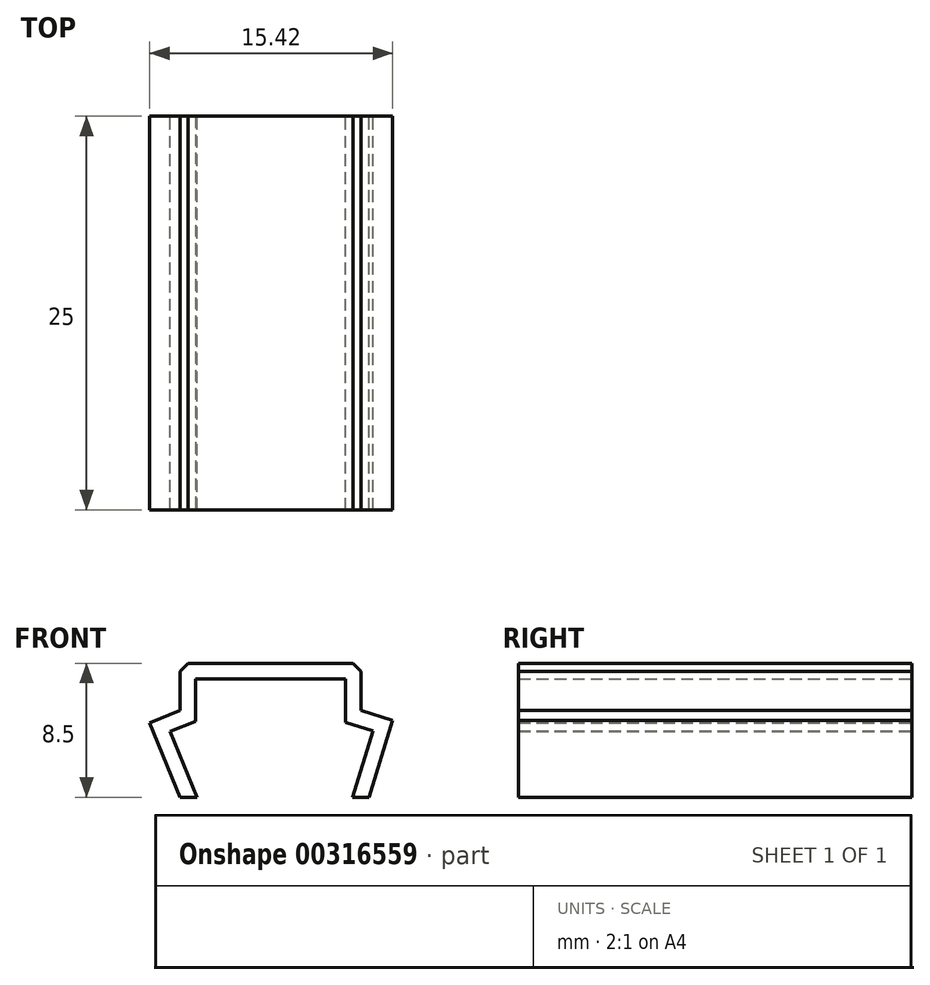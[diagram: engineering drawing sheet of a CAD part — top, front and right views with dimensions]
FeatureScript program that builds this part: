
annotation { "Feature Type Name" : "Feature", "Feature Type Description" : "" }
export const myFeature = defineFeature(function(context is Context, id is Id, definition is map)
    precondition{}
    {
        {
            var Q0;
            Q0=qCreatedBy(makeId("Front.planeOp"),FACE);
            var sketch = newSketch(context, id + "F0", { "sketchPlane" : qUnion([Q0])});
            skLineSegment(sketch, "E0.bottom", {"start": v(-0.8, 8.5) * mm, "end": v(9.7, 8.5) * mm});
            skLineSegment(sketch, "E0.left", {"start": v(-1.3, 8) * mm, "end": v(-1.3, 5.5) * mm});
            skLineSegment(sketch, "E0.right", {"start": v(10.2, 8) * mm, "end": v(10.2, 5.5) * mm});
            skLineSegment(sketch, "E1.top", {"start": v(-1.3, 0) * mm, "end": v(10.7, 0) * mm});
            skLineSegment(sketch, "E2", {"start": v(-3.23, 4.72) * mm, "end": v(-1.3, 0) * mm});
            skLineSegment(sketch, "E3", {"start": v(-1.3, 5.5) * mm, "end": v(-3.23, 4.72) * mm});
            skLineSegment(sketch, "E4", {"start": v(10.2, 5.5) * mm, "end": v(12.2, 4.89) * mm});
            skLineSegment(sketch, "E5", {"start": v(12.2, 4.89) * mm, "end": v(10.7, 0) * mm});
            skLineSegment(sketch, "E6", {"start": v(-1.3, 8) * mm, "end": v(-0.8, 8.5) * mm});
            skLineSegment(sketch, "E7", {"start": v(9.7, 8.5) * mm, "end": v(10.2, 8) * mm});
            skSolve(sketch);
        }
        {
            var Q0;
            Q0=makeQuery(id+"F0.imprint","IMPRINT",FACE,{"disambiguationData":[TD([[makeQuery(id+"F0.imprint","IMPRINT",EDGE,{"derivedFrom":sQuery(id+"F0.wireOp",EDGE,"E0.bottom")}),-1.0]])]});
            extrude(context, id + "F1", {"entities" : qUnion([Q0]), "depth" : 25 * mm});
        }
        {
            var Q0;
            Q0=makeQuery(id+"F1.opExtrude","CAP_FACE",FACE,{"disambiguationData":[OSD([sQuery(id+"F0.wireOp",EDGE,"E0.bottom"),sQuery(id+"F0.wireOp",EDGE,"E0.left"),sQuery(id+"F0.wireOp",EDGE,"E0.right"),sQuery(id+"F0.wireOp",EDGE,"E1.bottom"),sQuery(id+"F0.wireOp",EDGE,"E1.top"),sQuery(id+"F0.wireOp",EDGE,"0d6bb723-9a7b-4d77-b57e-2279504a17e3.trimOffspring"),sQuery(id+"F0.wireOp",EDGE,"19e43eaa-ee09-435e-811b-5a9f896a7d2e.filletArc"),sQuery(id+"F0.wireOp",EDGE,"6ffb7b8e-48f9-446f-8dbe-ae3deb286622.filletArc"),sQuery(id+"F0.wireOp",EDGE,"E2"),sQuery(id+"F0.wireOp",EDGE,"KxVvcCu0-cP9C-hDc2-rJ1g-qD9v42R25ilj")])],"isStart":false});
            var Q1;
            Q1=makeQuery(id+"F1.opExtrude","SWEPT_FACE",FACE,{"disambiguationData":[OSD([sQuery(id+"F0.wireOp",EDGE,"E1.top")])]});
            var Q2;
            Q2=makeQuery(id+"F1.opExtrude","CAP_FACE",FACE,{"disambiguationData":[OSD([sQuery(id+"F0.wireOp",EDGE,"E0.bottom"),sQuery(id+"F0.wireOp",EDGE,"E0.left"),sQuery(id+"F0.wireOp",EDGE,"E0.right"),sQuery(id+"F0.wireOp",EDGE,"E1.bottom"),sQuery(id+"F0.wireOp",EDGE,"E1.top"),sQuery(id+"F0.wireOp",EDGE,"0d6bb723-9a7b-4d77-b57e-2279504a17e3.trimOffspring"),sQuery(id+"F0.wireOp",EDGE,"19e43eaa-ee09-435e-811b-5a9f896a7d2e.filletArc"),sQuery(id+"F0.wireOp",EDGE,"6ffb7b8e-48f9-446f-8dbe-ae3deb286622.filletArc"),sQuery(id+"F0.wireOp",EDGE,"E2"),sQuery(id+"F0.wireOp",EDGE,"KxVvcCu0-cP9C-hDc2-rJ1g-qD9v42R25ilj")])],"isStart":true});
            var Q3;
            Q3=makeQuery(id+"F1.opExtrude","SWEPT_BODY",BODY,{"disambiguationData":[OSD([sQuery(id+"F0.wireOp",EDGE,"E0.bottom"),sQuery(id+"F0.wireOp",EDGE,"E0.left"),sQuery(id+"F0.wireOp",EDGE,"E0.right"),sQuery(id+"F0.wireOp",EDGE,"E1.bottom"),sQuery(id+"F0.wireOp",EDGE,"E1.top"),sQuery(id+"F0.wireOp",EDGE,"0d6bb723-9a7b-4d77-b57e-2279504a17e3.trimOffspring"),sQuery(id+"F0.wireOp",EDGE,"19e43eaa-ee09-435e-811b-5a9f896a7d2e.filletArc"),sQuery(id+"F0.wireOp",EDGE,"6ffb7b8e-48f9-446f-8dbe-ae3deb286622.filletArc"),sQuery(id+"F0.wireOp",EDGE,"E2"),sQuery(id+"F0.wireOp",EDGE,"KxVvcCu0-cP9C-hDc2-rJ1g-qD9v42R25ilj")])]});
            shell(context, id + "F2", {"entities" : qUnion([Q0, Q1, Q2]), "parts" : qUnion([Q3]), "thickness" : 1 * mm});
        }
    });
